# Revit family: sh-8834
name_source: partatom
category: Lighting Fixtures
revit_build: Autodesk Revit 2017 (Build: 20160225_1515(x64)
units: mm (PartAtom-declared; Revit-internal decimal feet)

## family parameters
Always vertical = Yes
Cut with Voids When Loaded = No
Host = Wall
Light Source = No
OmniClass Number = 23.80.70.00
OmniClass Title = Lighting
Part Type = Normal
Room Calculation Point = No
Round Connector Dimension = Use Diameter
Shared = Yes

## types (3) — shared parameters
Body Material = Aluminium
Cost = 1 $
Cunsumption current = 0 A
Flicker = Free Flicker
Height = 15.8 cm
IP = 65
Lamp = GU10
Manufacturer = SHOA
Model = SH-8834
Protection Class = class I
Type medule = smd
URL = https://www.shoaco.com
Voltage/Frequency = 230 V Ac/50HZ
Website = www.shoaco.com
Width = 12.6 cm
color temperature = 3000K
instalation = Wall Mounted
wattage. = 14 W

## per-type parameters (varying)
| type | Body color | color rendering index(CRI) |
| SH-8834( Black body-GU10) | Black | 90 |
| SH-8834(white body-GU10) | White | 80 |
| SH-8834(Gray body-GU10) | Gray | 80 |

## geometry (parser evidence)
native form markers: Sweep x5
no freeform markers — native parametric forms only
